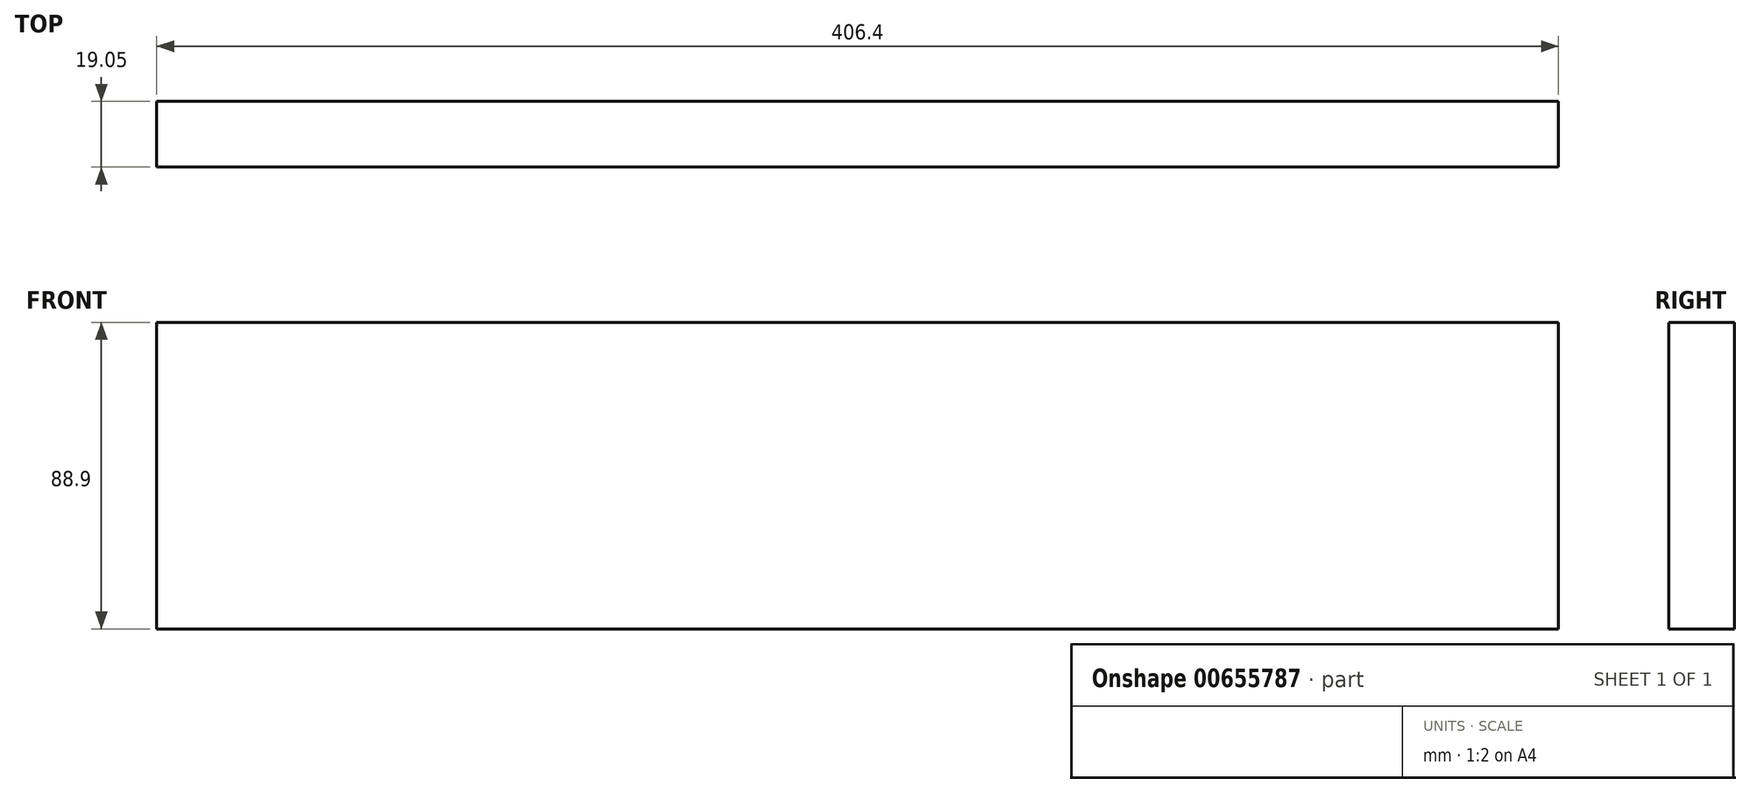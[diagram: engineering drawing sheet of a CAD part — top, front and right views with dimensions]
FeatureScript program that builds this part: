
annotation { "Feature Type Name" : "Feature", "Feature Type Description" : "" }
export const myFeature = defineFeature(function(context is Context, id is Id, definition is map)
    precondition{}
    {
        {
            var Q0;
            Q0=qCreatedBy(makeId("Front.planeOp"),FACE);
            var sketch = newSketch(context, id + "F0", { "sketchPlane" : qUnion([Q0])});
            skLineSegment(sketch, "E0.bottom", {"start": v(203.2, 44.45) * mm, "end": v(-203.2, 44.45) * mm});
            skLineSegment(sketch, "E0.top", {"start": v(203.2, -44.45) * mm, "end": v(-203.2, -44.45) * mm});
            skLineSegment(sketch, "E0.left", {"start": v(203.2, 44.45) * mm, "end": v(203.2, -44.45) * mm});
            skLineSegment(sketch, "E0.right", {"start": v(-203.2, 44.45) * mm, "end": v(-203.2, -44.45) * mm});
            skPoint(sketch, "E0.middle", {"position": v(0, 0) * mm});
            skSolve(sketch);
        }
        {
            var Q0;
            Q0=makeQuery(id+"F0.imprint","IMPRINT",FACE,{"disambiguationData":[TD([[makeQuery(id+"F0.imprint","IMPRINT",EDGE,{"derivedFrom":sQuery(id+"F0.wireOp",EDGE,"E0.bottom")}),1.0]])]});
            extrude(context, id + "F1", {"entities" : qUnion([Q0]), "depth" : 19.05 * mm, "offsetDistance" : 25.4 * mm});
        }
    });
